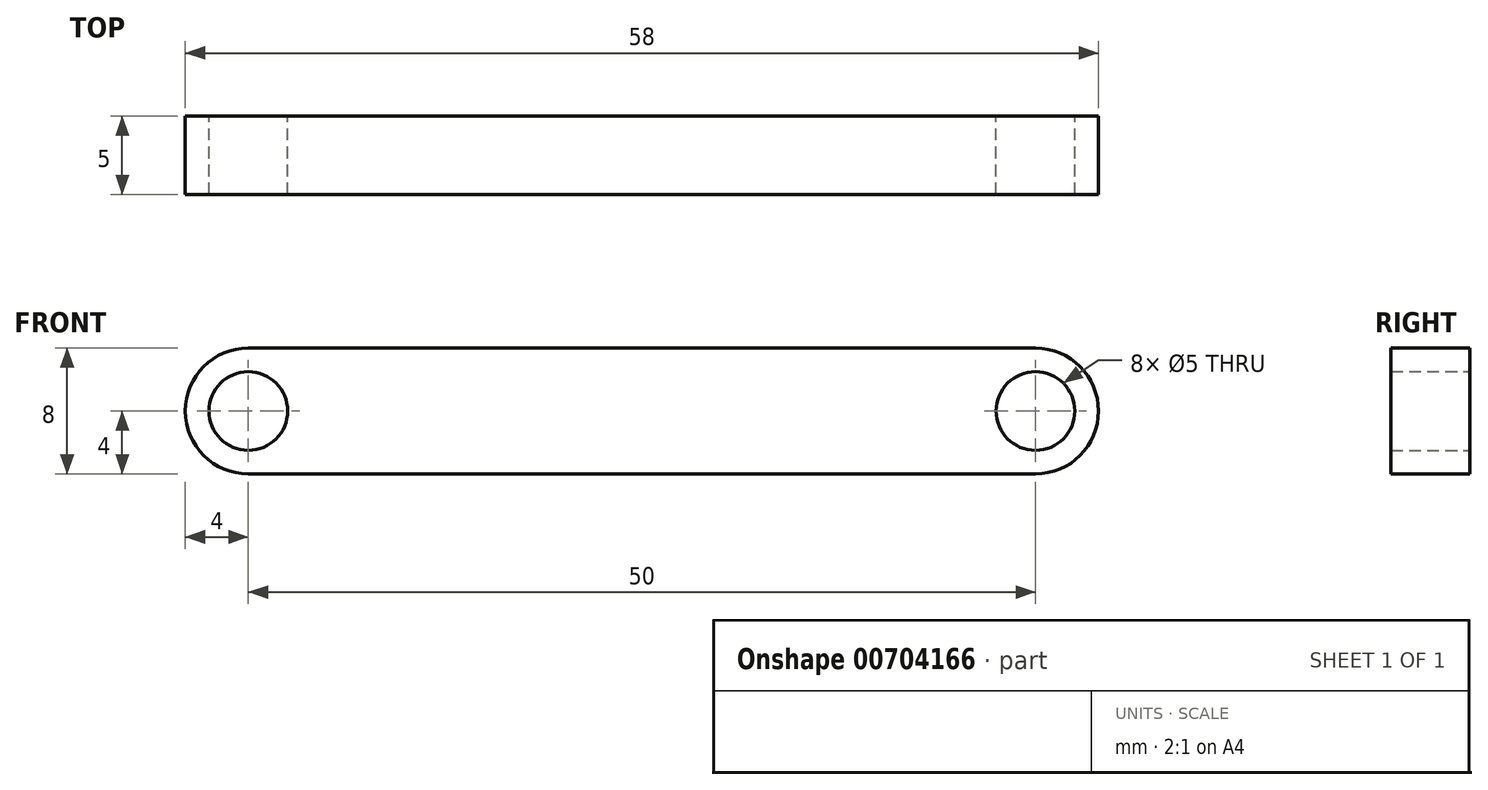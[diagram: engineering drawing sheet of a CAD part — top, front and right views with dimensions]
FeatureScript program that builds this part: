
annotation { "Feature Type Name" : "Feature", "Feature Type Description" : "" }
export const myFeature = defineFeature(function(context is Context, id is Id, definition is map)
    precondition{}
    {
        {
            var Q0;
            Q0=qCreatedBy(makeId("Front.planeOp"),FACE);
            var sketch = newSketch(context, id + "F0", { "sketchPlane" : qUnion([Q0])});
            skLineSegment(sketch, "E0.bottom", {"start": v(-25, 4) * mm, "end": v(0, 4) * mm});
            skLineSegment(sketch, "E0.top", {"start": v(-25, -4) * mm, "end": v(0, -4) * mm});
            skLineSegment(sketch, "E0.left", {"start": v(-25, 4) * mm, "end": v(-25, -4) * mm, "construction": true});
            skLineSegment(sketch, "E0.right", {"start": v(0, 4) * mm, "end": v(0, -4) * mm});
            skArc(sketch, "E1", {"start": v(-25, -4) * mm, "mid": v(-29, 0) * mm, "end": v(-25, 4) * mm});
            skCircle(sketch, "E2", {"center": v(-25, 0) * mm, "radius": 2.5 * mm});
            skLineSegment(sketch, "E3.MirrorCS", {"start": v(25, -4) * mm, "end": v(0, -4) * mm});
            skArc(sketch, "E4.MirrorCS", {"start": v(25, -4) * mm, "mid": v(29, 0) * mm, "end": v(25, 4) * mm});
            skCircle(sketch, "E5.MirrorC", {"center": v(25, 0) * mm, "radius": 2.5 * mm});
            skLineSegment(sketch, "E6.MirrorCS", {"start": v(25, 4) * mm, "end": v(0, 4) * mm});
            skSolve(sketch);
        }
        {
            var Q0;
            Q0=makeQuery(id+"F0.imprint","IMPRINT",FACE,{"disambiguationData":[TD([[makeQuery(id+"F0.imprint","IMPRINT",EDGE,{"derivedFrom":sQuery(id+"F0.wireOp",EDGE,"E0.bottom")}),-1.0]])]});
            var Q1;
            Q1=makeQuery(id+"F0.imprint","IMPRINT",FACE,{"disambiguationData":[TD([[makeQuery(id+"F0.imprint","IMPRINT",EDGE,{"derivedFrom":sQuery(id+"F0.wireOp",EDGE,"E0.right")}),1.0]])]});
            extrude(context, id + "F1", {"entities" : qUnion([Q0, Q1]), "depth" : 5 * mm, "offsetDistance" : 25 * mm});
        }
    });
